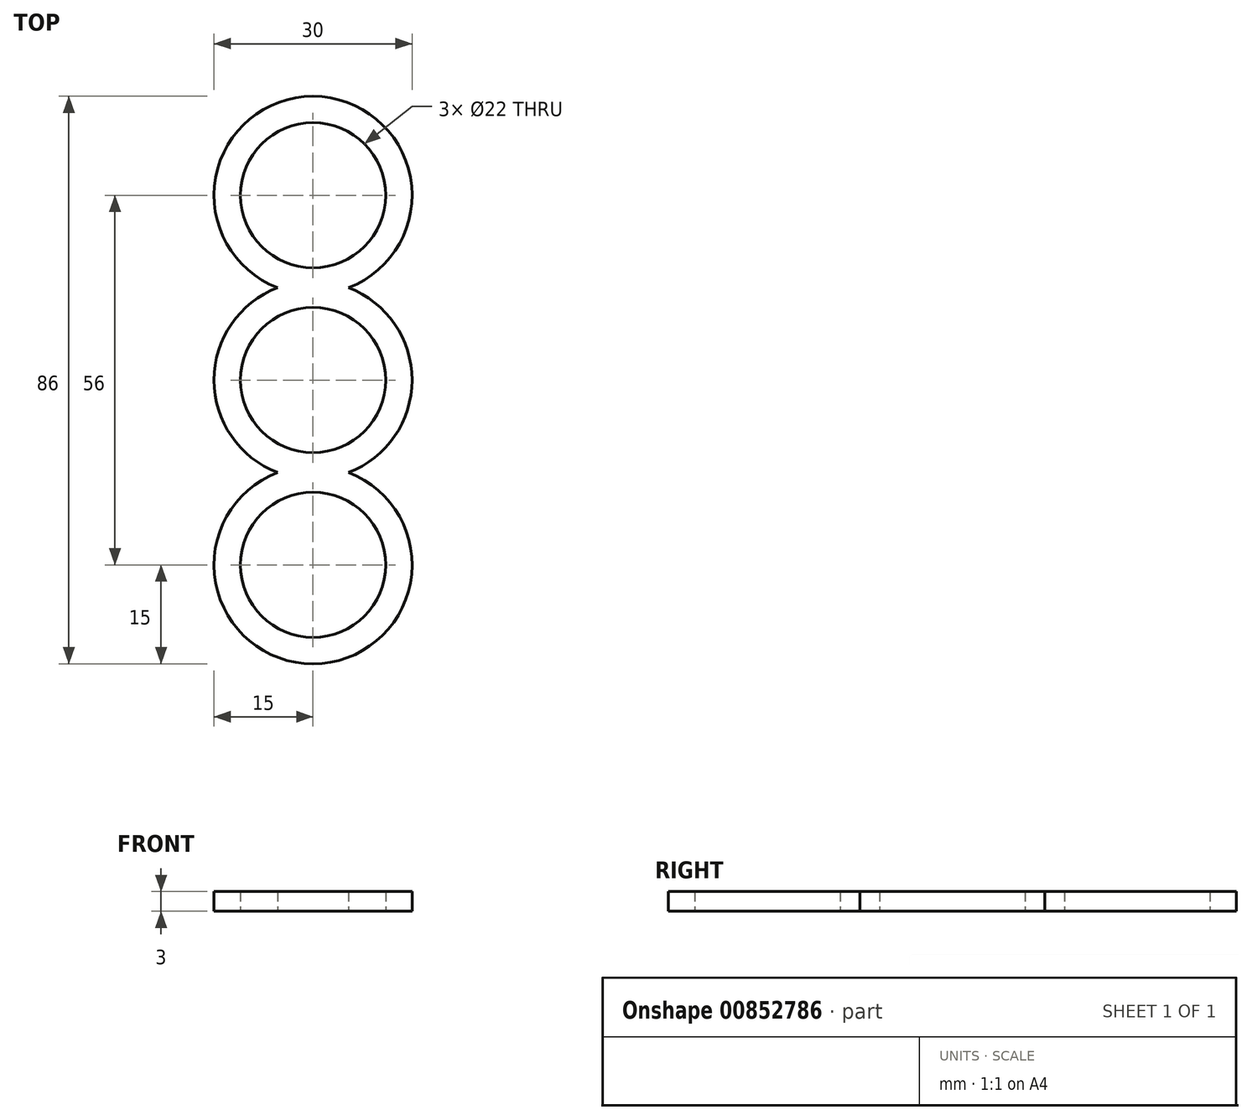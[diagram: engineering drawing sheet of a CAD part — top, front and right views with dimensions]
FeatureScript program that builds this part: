
annotation { "Feature Type Name" : "Feature", "Feature Type Description" : "" }
export const myFeature = defineFeature(function(context is Context, id is Id, definition is map)
    precondition{}
    {
        {
            var Q0;
            Q0=qCreatedBy(makeId("Top.planeOp"),FACE);
            var sketch = newSketch(context, id + "F0", { "sketchPlane" : qUnion([Q0])});
            skCircle(sketch, "E0", {"center": v(0, 0) * mm, "radius": 11 * mm});
            skArc(sketch, "E1", {"start": v(-5.39, 14) * mm, "mid": v(-15, 0) * mm, "end": v(-5.39, -14) * mm});
            skCircle(sketch, "E2", {"center": v(0, 28) * mm, "radius": 11 * mm});
            skArc(sketch, "E3", {"start": v(5.39, 14) * mm, "mid": v(0, 43) * mm, "end": v(-5.39, 14) * mm});
            skCircle(sketch, "E4", {"center": v(0, -28) * mm, "radius": 11 * mm});
            skArc(sketch, "E5", {"start": v(-5.39, -14) * mm, "mid": v(0, -43) * mm, "end": v(5.39, -14) * mm});
            skArc(sketch, "E6.trimOffspring", {"start": v(5.39, -14) * mm, "mid": v(15, 0) * mm, "end": v(5.39, 14) * mm});
            skSolve(sketch);
        }
        {
            var Q0;
            Q0=qSketchRegion(id+"F0",true);
            extrude(context, id + "F1", {"entities" : qUnion([Q0]), "depth" : 3 * mm, "offsetDistance" : 25 * mm});
        }
    });
